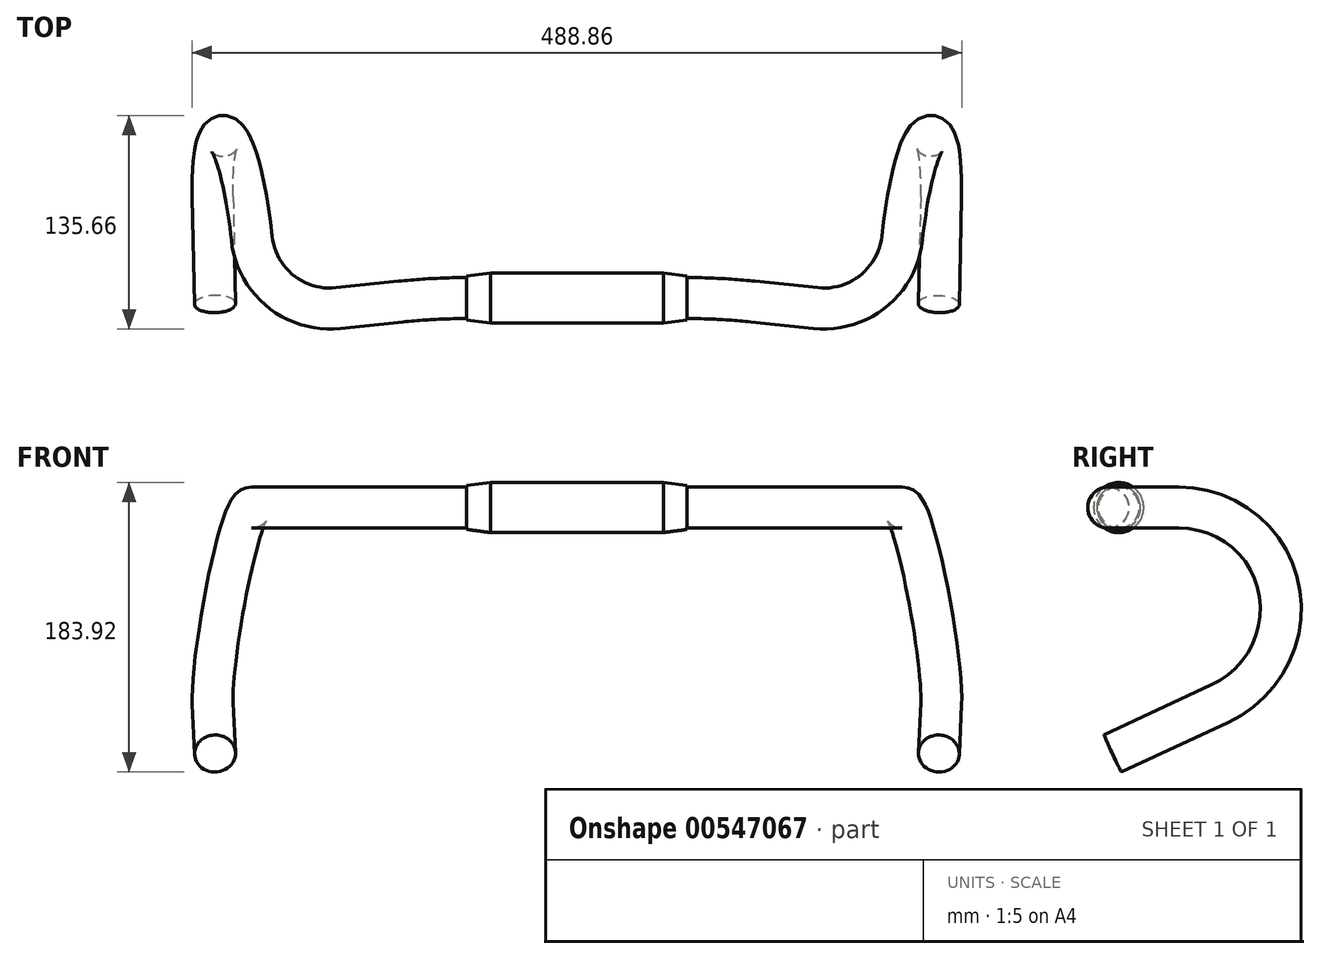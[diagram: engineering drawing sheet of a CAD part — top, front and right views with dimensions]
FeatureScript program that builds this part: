
annotation { "Feature Type Name" : "Feature", "Feature Type Description" : "" }
export const myFeature = defineFeature(function(context is Context, id is Id, definition is map)
    precondition{}
    {
        {
            var Q0;
            Q0=qCreatedBy(makeId("Right.planeOp"),FACE);
            var sketch = newSketch(context, id + "F0", { "sketchPlane" : qUnion([Q0])});
            skCircle(sketch, "E0", {"center": v(0, 0) * mm, "radius": 15.9 * mm});
            skCircle(sketch, "E1", {"center": v(0, 0) * mm, "radius": 13 * mm});
            skLineSegment(sketch, "E2", {"start": v(68.88, 32.12) * mm, "end": v(128.05, -94.76) * mm, "construction": true});
            skLineSegment(sketch, "E3", {"start": v(1.16, -153.93) * mm, "end": v(128.05, -94.76) * mm, "construction": true});
            skLineSegment(sketch, "E4", {"start": v(0, 0) * mm, "end": v(50, 0) * mm, "construction": true});
            skLineSegment(sketch, "E5", {"start": v(0, 0) * mm, "end": v(68.88, 32.12) * mm, "construction": true});
            skSolve(sketch);
        }
        {
            var Q0;
            Q0=qCreatedBy(makeId("Top.planeOp"),FACE);
            var sketch = newSketch(context, id + "F1", { "sketchPlane" : qUnion([Q0])});
            skLineSegment(sketch, "E6", {"start": v(0, 0) * mm, "end": v(70, 0) * mm});
            skLineSegment(sketch, "E7", {"start": v(111.81, -2.2) * mm, "end": v(151.6, -6.37) * mm});
            skPoint(sketch, "E8.visualSharp", {"position": v(90.96, 0) * mm});
            skArc(sketch, "E8.filletArc", {"start": v(111.81, -2.2) * mm, "mid": v(90.93, -0.55) * mm, "end": v(70, 0) * mm});
            skArc(sketch, "E9", {"start": v(151.6, -6.37) * mm, "mid": v(188.28, 4.5) * mm, "end": v(206.54, 38.13) * mm});
            skLineSegment(sketch, "E10", {"start": v(156.82, 43.35) * mm, "end": v(151.6, -6.37) * mm, "construction": true});
            skLineSegment(sketch, "E11", {"start": v(156.82, 43.35) * mm, "end": v(206.54, 38.13) * mm, "construction": true});
            skSolve(sketch);
        }
        {
            var Q0;
            Q0=sQuery(id+"F0.wireOp",EDGE,"E5");
            var Q1;
            Q1=sQuery(id+"F0.wireOp",VERTEX,"E5.end");
            cPlane(context, id + "F2", {"entities" : qUnion([Q0, Q1]), "cplaneType" : CPlaneType.LINE_POINT, "offset" : 25 * mm, "width" : 150 * mm, "height" : 150 * mm});
        }
        {
            var Q0;
            Q0=sQuery(id+"F0.wireOp",EDGE,"E2");
            var Q1;
            Q1=sQuery(id+"F0.wireOp",VERTEX,"E3.end");
            cPlane(context, id + "F3", {"entities" : qUnion([Q0, Q1]), "cplaneType" : CPlaneType.LINE_POINT, "offset" : 25 * mm, "width" : 150 * mm, "height" : 150 * mm});
        }
        {
            var Q0;
            Q0=sQuery(id+"F1.wireOp",EDGE,"E9");
            var Q1;
            Q1=sQuery(id+"F1.wireOp",VERTEX,"E11.end");
            cPlane(context, id + "F4", {"entities" : qUnion([Q0, Q1]), "cplaneType" : CPlaneType.CURVE_POINT, "offset" : 25 * mm, "width" : 150 * mm, "height" : 150 * mm});
        }
        {
            var Q0;
            Q0=qCreatedBy(id+"F4.planeOp",FACE);
            var sketch = newSketch(context, id + "F5", { "sketchPlane" : qUnion([Q0])});
            skLineSegment(sketch, "E12.0", {"start": v(-151.43, 0) * mm, "end": v(-201.43, 0) * mm});
            skLineSegment(sketch, "E13", {"start": v(-201.43, 0) * mm, "end": v(-152.19, -8.68) * mm, "construction": true});
            skSolve(sketch);
        }
        {
            var Q0;
            Q0=sQuery(id+"F5.wireOp",EDGE,"E13");
            var Q1;
            Q1=sQuery(id+"F5.wireOp",VERTEX,"E13.start");
            cPlane(context, id + "F6", {"entities" : qUnion([Q0, Q1]), "cplaneType" : CPlaneType.LINE_POINT, "offset" : 25 * mm, "width" : 150 * mm, "height" : 150 * mm});
        }
        {
            var Q0;
            Q0=qCreatedBy(id+"F6.planeOp",FACE);
            var sketch = newSketch(context, id + "F7", { "sketchPlane" : qUnion([Q0])});
            skLineSegment(sketch, "E14", {"start": v(-157.49, -151.92) * mm, "end": v(-72.4, 33.96) * mm, "construction": true});
            skLineSegment(sketch, "E15", {"start": v(20.86, -210.98) * mm, "end": v(-164.43, -127.08) * mm, "construction": true});
            skPoint(sketch, "E16.0", {"position": v(-58.86, -36.06) * mm});
            skEllipticalArc(sketch, "E17.0", {"construction": true});
            skLineSegment(sketch, "E18", {"start": v(-58.86, -36.06) * mm, "end": v(-4.55, -35.07) * mm, "construction": true});
            skArc(sketch, "E19", {"start": v(-58.86, -36.06) * mm, "mid": v(-122.72, -89.07) * mm, "end": v(-85.06, -163.02) * mm});
            skLineSegment(sketch, "E20", {"start": v(-85.06, -163.02) * mm, "end": v(-16.73, -193.96) * mm});
            skLineSegment(sketch, "E21", {"start": v(-16.73, -193.96) * mm, "end": v(-85.06, -163.02) * mm});
            const initialGuessF7  = {"E17.0": [-0.04397766391466506, -0.026882655366650465, 0.9999954064292567, 0.003031026292545284, 0.05, 0.008682408883346504, 4.71238898038469, 0.0872664625997145]};
            skSetInitialGuess(sketch, initialGuessF7);
            skSolve(sketch);
        }
        {
            var Q0;
            Q0=makeQuery(id+"F0.imprint","IMPRINT",FACE,{"disambiguationData":[TD([[makeQuery(id+"F0.imprint","IMPRINT",EDGE,{"derivedFrom":sQuery(id+"F0.wireOp",EDGE,"E1")}),1.0]])]});
            var Q1;
            Q1=sQuery(id+"F7.wireOp",EDGE,"E21");
            var Q2;
            Q2=sQuery(id+"F7.wireOp",EDGE,"E19");
            var Q3;
            Q3=sQuery(id+"F1.wireOp",EDGE,"E9");
            var Q4;
            Q4=sQuery(id+"F1.wireOp",EDGE,"E7");
            var Q5;
            Q5=sQuery(id+"F1.wireOp",EDGE,"E8.filletArc");
            var Q6;
            Q6=sQuery(id+"F1.wireOp",EDGE,"E6");
            sweep(context, id + "F8", {"profiles" : qUnion([Q0]), "path" : qUnion([Q1, Q2, Q3, Q4, Q5, Q6])});
        }
        {
            var Q0;
            Q0=makeQuery(id+"F0.imprint","IMPRINT",FACE,{"disambiguationData":[TD([[makeQuery(id+"F0.imprint","IMPRINT",EDGE,{"derivedFrom":sQuery(id+"F0.wireOp",EDGE,"E0")}),1.0]])]});
            extrude(context, id + "F9", {"entities" : qUnion([Q0]), "operationType" : NewBodyOperationType.ADD, "depth" : 70 * mm, "offsetDistance" : 25 * mm});
        }
        {
            var Q0;
            Q0=makeQuery(id+"F9.opExtrude","CAP_EDGE",EDGE,{"disambiguationData":[OSD([sQuery(id+"F0.wireOp",EDGE,"E0")])],"isStart":false});
            chamfer(context, id + "F10", {"entities" : qUnion([Q0]), "chamferType" : ChamferType.TWO_OFFSETS, "width1" : 2 * mm, "oppositeDirection" : false, "width2" : 15 * mm, "tangentPropagation" : true});
        }
        {
            var Q0;
            Q0=makeQuery(id+"F8.opSweep","SWEPT_BODY",BODY,{"disambiguationData":[OSD([sQuery(id+"F0.wireOp",EDGE,"E1"),sQuery(id+"FU3fFmzONj8psco_0.wireOp",EDGE,"5ce3c69e-82f7-4cf6-a305-a2685bf24168.0")])]});
            var Q1;
            Q1=qCreatedBy(makeId("Right.planeOp"),FACE);
            mirror(context, id + "F11", {"operationType" : NewBodyOperationType.ADD, "entities" : qUnion([Q0]), "mirrorPlane" : qUnion([Q1])});
        }
    });
